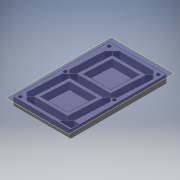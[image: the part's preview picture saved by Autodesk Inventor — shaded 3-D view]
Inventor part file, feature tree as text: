
AUTODESK INVENTOR PART (.ipt)
format: ipt  version: 2016 SP2 (Build 200236200, 236)  size: 308,736 bytes
history: native  units: mm
features: reference x11, extrude x4, sketch x4, plane x1
ambient origin geometry x8: Origin, YZ Plane, XZ Plane, XY Plane, X Axis, Y Axis, Z Axis, Center Point
bodies: Volumenkörper1 (feature_tree)
feature tree (20):
  plane  "Arbeitsebene1"
  extrude  "Extrusion1"  Depth=10.5mm
  extrude  "Extrusion2"  Depth=3.5mm
  extrude  "Extrusion3"  Depth=3.5mm
  extrude  "Extrusion4"  Depth=3.0mm
  sketch  "Skizze1"  dims[d0=10.5mm d1=0.0mm d2=3.5mm]
  reference  "Referenz1"
  sketch  "Skizze2"  dims[d3=3.5mm d4=3.5mm]
  sketch  "Skizze3"  dims[d5=3.5mm d6=3.5mm]
  reference  "Referenz2"
  reference  "Referenz3"
  reference  "Referenz4"
  reference  "Referenz5"
  reference  "Referenz6"
  sketch  "Skizze4"  dims[d7=3.5mm d8=3.5mm d9=3.5mm d10=3.5mm d11=3.5mm d12=3.5mm d13=3.5mm d14=3.5mm d15=3.5mm d16=3.5mm d17=3.5mm d18=1.7mm d19=1.7mm d20=1.7mm d21=1.7mm d22=1.7mm d23=1.7mm d24=1.7mm d25=1.7mm d26=1.7mm d27=1.7mm d28=1.7mm d29=1.7mm d30=1.7mm d31=1.7mm d32=1.7mm d33=1.7mm d34=1.7mm d35=1.7mm d36=0.8mm d37=0.8mm d38=0.8mm d39=0.8mm d40=0.8mm d41=0.8mm d42=0.8mm d43=0.8mm d44=0.8mm d45=0.8mm d46=0.8mm d47=0.8mm d48=0.8mm d49=0.8mm d50=0.8mm d51=0.0mm d52=3.0mm d53=0.0mm d54=3.0mm d55=0.0mm]
  reference  "Referenz7"
  reference  "Referenz8"
  reference  "Referenz9"
  reference  "Referenz10"
  reference  "Referenz11"
